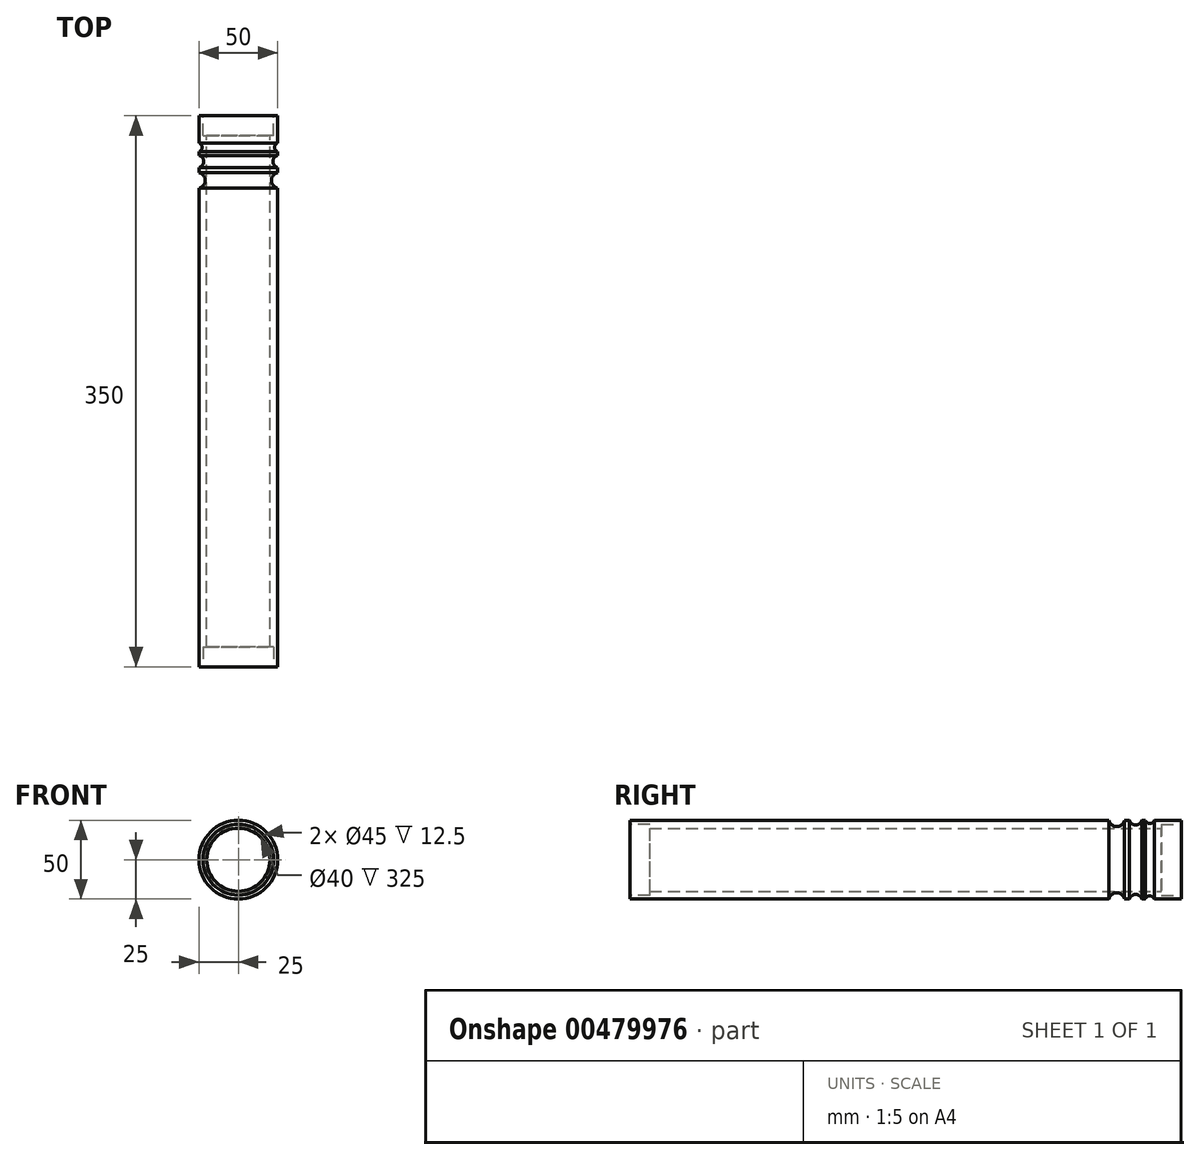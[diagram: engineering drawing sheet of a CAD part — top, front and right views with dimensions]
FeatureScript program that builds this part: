
annotation { "Feature Type Name" : "Feature", "Feature Type Description" : "" }
export const myFeature = defineFeature(function(context is Context, id is Id, definition is map)
    precondition{}
    {
        {
            var Q0;
            Q0=qCreatedBy(makeId("Front.planeOp"),FACE);
            var sketch = newSketch(context, id + "F0", { "sketchPlane" : qUnion([Q0])});
            skCircle(sketch, "E0", {"center": v(0, 0) * mm, "radius": 25 * mm});
            skCircle(sketch, "E1", {"center": v(0, 0) * mm, "radius": 20 * mm});
            skSolve(sketch);
        }
        {
            var Q0;
            Q0=makeQuery(id+"F0.imprint","IMPRINT",FACE,{"disambiguationData":[TD([[makeQuery(id+"F0.imprint","IMPRINT",EDGE,{"derivedFrom":sQuery(id+"F0.wireOp",EDGE,"E0")}),1.0]])]});
            extrude(context, id + "F1", {"entities" : qUnion([Q0]), "depth" : 350 * mm});
        }
        {
            var Q0;
            Q0=makeQuery(id+"F1.opExtrude","CAP_FACE",FACE,{"disambiguationData":[OSD([sQuery(id+"F0.wireOp",EDGE,"E0"),sQuery(id+"F0.wireOp",EDGE,"E1")])],"isStart":false});
            var sketch = newSketch(context, id + "F2", { "sketchPlane" : qUnion([Q0])});
            skCircle(sketch, "E2", {"center": v(0, 0) * mm, "radius": 22.5 * mm});
            skSolve(sketch);
        }
        {
            var Q0;
            Q0=makeQuery(id+"F2.imprint","IMPRINT",FACE,{"disambiguationData":[TD([[makeQuery(id+"F2.imprint","IMPRINT",EDGE,{"derivedFrom":sQuery(id+"F2.wireOp",EDGE,"E2")}),1.0]])]});
            extrude(context, id + "F3", {"entities" : qUnion([Q0]), "operationType" : NewBodyOperationType.REMOVE, "oppositeDirection" : true, "depth" : 12.5 * mm});
        }
        {
            var Q0;
            Q0=makeQuery(id+"F1.opExtrude","CAP_FACE",FACE,{"disambiguationData":[OSD([sQuery(id+"F0.wireOp",EDGE,"E0"),sQuery(id+"F0.wireOp",EDGE,"E1")])],"isStart":true});
            var sketch = newSketch(context, id + "F4", { "sketchPlane" : qUnion([Q0])});
            skCircle(sketch, "E3", {"center": v(0, 0) * mm, "radius": 22.5 * mm});
            skSolve(sketch);
        }
        {
            var Q0;
            Q0=makeQuery(id+"F4.imprint","IMPRINT",FACE,{"disambiguationData":[TD([[makeQuery(id+"F4.imprint","IMPRINT",EDGE,{"derivedFrom":sQuery(id+"F4.wireOp",EDGE,"E3")}),1.0]])]});
            extrude(context, id + "F5", {"entities" : qUnion([Q0]), "operationType" : NewBodyOperationType.REMOVE, "oppositeDirection" : true, "depth" : 12.5 * mm});
        }
        {
            var Q0;
            Q0=qCreatedBy(makeId("Right.planeOp"),FACE);
            var sketch = newSketch(context, id + "F6", { "sketchPlane" : qUnion([Q0])});
            skCircle(sketch, "E4", {"center": v(-20, 26) * mm, "radius": 3 * mm});
            skCircle(sketch, "E5", {"center": v(-29, 26) * mm, "radius": 4 * mm});
            skCircle(sketch, "E6", {"center": v(-41, 26) * mm, "radius": 5 * mm});
            skSolve(sketch);
        }
        {
            var Q0;
            Q0=makeQuery(id+"F6.imprint","IMPRINT",FACE,{"disambiguationData":[TD([[makeQuery(id+"F6.imprint","IMPRINT",EDGE,{"derivedFrom":sQuery(id+"F6.wireOp",EDGE,"E4")}),1.0]])]});
            var Q1;
            Q1=makeQuery(id+"F6.imprint","IMPRINT",FACE,{"disambiguationData":[TD([[makeQuery(id+"F6.imprint","IMPRINT",EDGE,{"derivedFrom":sQuery(id+"F6.wireOp",EDGE,"E5")}),1.0]])]});
            var Q2;
            Q2=makeQuery(id+"F6.imprint","IMPRINT",FACE,{"disambiguationData":[TD([[makeQuery(id+"F6.imprint","IMPRINT",EDGE,{"derivedFrom":sQuery(id+"F6.wireOp",EDGE,"E6")}),1.0]])]});
            var Q3;
            Q3=makeQuery(id+"F1.opExtrude","SWEPT_FACE",FACE,{"disambiguationData":[OSD([sQuery(id+"F0.wireOp",EDGE,"E1")])]});
            revolve(context, id + "F7", {"operationType" : NewBodyOperationType.REMOVE, "entities" : qUnion([Q0, Q1, Q2]), "axis" : qUnion([Q3]), "revolveType" : RevolveType.FULL, "oppositeDirection" : true});
        }
    });
